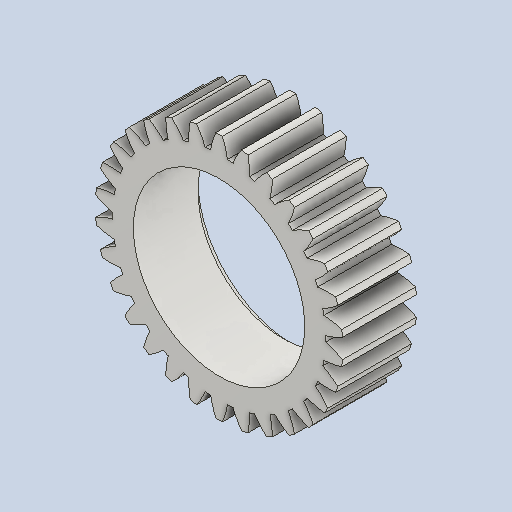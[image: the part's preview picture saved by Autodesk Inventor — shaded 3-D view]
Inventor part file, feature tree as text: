
AUTODESK INVENTOR PART (.ipt)
format: ipt  version: 2022 (Build 260153000, 153)  size: 350,208 bytes
history: native  units: in
note: dims shown in document units (in); Inventor stores cm internally (conversion verified against a paired STEP export)
features: other x12, plane x4, sketch x3
ambient origin geometry x8: Origin, YZ Plane, XZ Plane, XY Plane, X Axis, Y Axis, Z Axis, Center Point
bodies: Solid1 (feature_tree)
feature tree (19):
  other  "Spur Gear1"
  other  "Solid1::Spur Gear1"
  other  "TaggingFeature1"
  sketch  "Sketch1"  dims[d0=0.3937in]
  sketch  "Sketch2"  dims[d9=0.0in]
  sketch  "Sketch3"  dims[d14=0.0in d15=1.0in d16=0.0in d17=0.0in d18=0.0in d19=1.0in]
  plane  "XZ Plane_1"
  plane  "Work Plane2"
  plane  "Work Plane3"
  plane  "Work Plane4"
  other  "Srf1"
  other  "Srf1::Derived"
  other  "Start plane iMate"
  other  "Distance iMate"
  other  "Position iMate"
  other  "Mesh iMate"
  other  "Axis iMate"
  other  "Mesh iMate2"
  other  "Align iMate"
